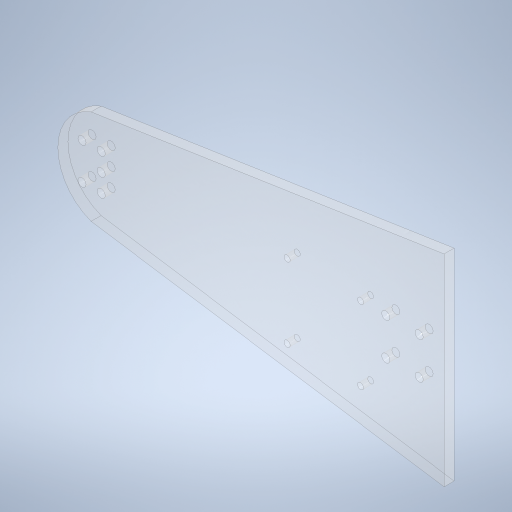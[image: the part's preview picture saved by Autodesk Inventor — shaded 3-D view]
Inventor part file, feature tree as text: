
AUTODESK INVENTOR PART (.ipt)
format: ipt  version: 2023.1 (Build 271208000, 208)  size: 307,200 bytes
history: native  units: in
note: dims shown in document units (in); Inventor stores cm internally (conversion verified against a paired STEP export)
features: reference x5, other x3, extrude x1, hole x1, sketch x1
ambient origin geometry x8: Origin, YZ Plane, XZ Plane, XY Plane, X Axis, Y Axis, Z Axis, Center Point
bodies: Solid1 (feature_tree)
feature tree (11):
  extrude  "Extrusion1"  Depth=0.9843in
  hole  "Hole1"  [1 undecoded]
  reference  "Reference2"
  reference  "Reference8"
  reference  "Reference9"
  reference  "Reference10"
  reference  "Reference11"
  sketch  "Sketch2"  dims[d0=3.937in d1=1.9685in d4=0.1969in d5=0.0in d7=0.1339in d8=0.1181in d9=0.0in d10=0.1181in d11=1.4409in d12=0.8504in d14=0.1181in d15=0.2362in d16=0.1575in d17=0.0787in d18=90.0deg d19=0.315in d20=0.8108in d24=1.9685in d25=0.9843in d27=0.0in d28=0.3543in d29=0.3543in d30=0.1575in d31=0.0in d32=0.0in]
  other  "Ensamble.iam"
  other  "base:1"
  other  "SoporteUnion:1"
note: 1 required parameter value undecoded (feature->parameter linkage not recoverable at this tier; creation-order binding heuristic only, values carry confidence <= 0.55)
